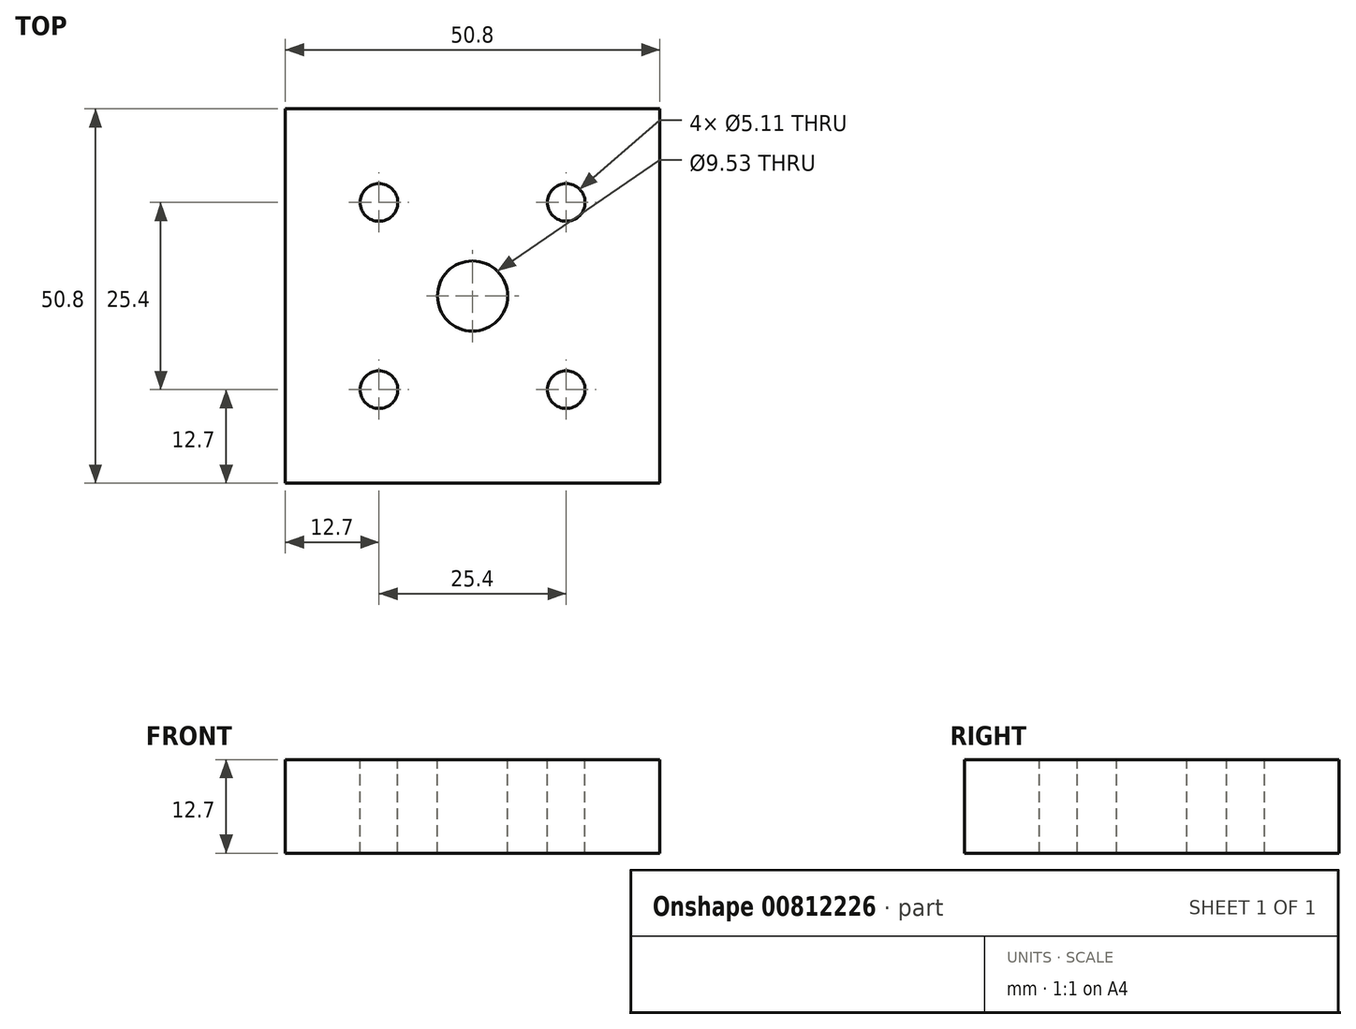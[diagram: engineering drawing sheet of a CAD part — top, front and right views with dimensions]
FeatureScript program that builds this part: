
annotation { "Feature Type Name" : "Feature", "Feature Type Description" : "" }
export const myFeature = defineFeature(function(context is Context, id is Id, definition is map)
    precondition{}
    {
        {
            var Q0;
            Q0=qCreatedBy(makeId("Front.planeOp"),FACE);
            var sketch = newSketch(context, id + "F0", { "sketchPlane" : qUnion([Q0])});
            skLineSegment(sketch, "E0.bottom", {"start": v(-25.4, 0) * mm, "end": v(25.4, 0) * mm});
            skLineSegment(sketch, "E0.top", {"start": v(-25.4, 12.7) * mm, "end": v(25.4, 12.7) * mm});
            skLineSegment(sketch, "E0.left", {"start": v(-25.4, 0) * mm, "end": v(-25.4, 12.7) * mm});
            skLineSegment(sketch, "E0.right", {"start": v(25.4, 0) * mm, "end": v(25.4, 12.7) * mm});
            skPoint(sketch, "E0.middle", {"position": v(0, 6.35) * mm});
            skSolve(sketch);
        }
        {
            var Q0;
            Q0 = qSketchRegion(id + "F0", true);
            extrude(context, id + "F1", {"entities" : qUnion([Q0]), "depth" : 50.8 * mm, "offsetDistance" : 25.4 * mm});
        }
        {
            var Q0;
            Q0=makeQuery(id+"F1.opExtrude","SWEPT_FACE",FACE,{"disambiguationData":[OSD([sQuery(id+"F0.wireOp",EDGE,"E0.top")])]});
            var sketch = newSketch(context, id + "F2", { "sketchPlane" : qUnion([Q0])});
            skLineSegment(sketch, "E1.bottom", {"start": v(-12.7, -12.7) * mm, "end": v(12.7, -12.7) * mm, "construction": true});
            skLineSegment(sketch, "E1.top", {"start": v(-12.7, -38.1) * mm, "end": v(12.7, -38.1) * mm, "construction": true});
            skLineSegment(sketch, "E1.left", {"start": v(-12.7, -12.7) * mm, "end": v(-12.7, -38.1) * mm, "construction": true});
            skLineSegment(sketch, "E1.right", {"start": v(12.7, -12.7) * mm, "end": v(12.7, -38.1) * mm, "construction": true});
            skPoint(sketch, "E1.middle", {"position": v(0, -25.4) * mm});
            skPoint(sketch, "E1.middle.positionSnap0", {"position": v(-25.4, -25.4) * mm});
            skPoint(sketch, "E1.centerSnap0", {"position": v(-25.4, -25.4) * mm});
            skCircle(sketch, "E2", {"center": v(-12.7, -12.7) * mm, "radius": 2.55 * mm});
            skCircle(sketch, "E3", {"center": v(-12.7, -38.1) * mm, "radius": 2.55 * mm});
            skCircle(sketch, "E4", {"center": v(12.7, -38.1) * mm, "radius": 2.55 * mm});
            skCircle(sketch, "E5", {"center": v(12.7, -12.7) * mm, "radius": 2.55 * mm});
            skCircle(sketch, "E6", {"center": v(0, -25.4) * mm, "radius": 4.76 * mm});
            skSolve(sketch);
        }
        {
            var Q0;
            Q0 = qSketchRegion(id + "F2", true);
            extrude(context, id + "F3", {"entities" : qUnion([Q0]), "operationType" : NewBodyOperationType.REMOVE, "endBound" : BoundingType.THROUGH_ALL, "oppositeDirection" : true, "depth" : 25.4 * mm, "offsetDistance" : 25.4 * mm});
        }
        {
            var Q0;
            Q0=makeQuery(id+"F1.opExtrude","SWEPT_FACE",FACE,{"disambiguationData":[OSD([sQuery(id+"F0.wireOp",EDGE,"E0.top")])]});
            var sketch = newSketch(context, id + "F4", { "sketchPlane" : qUnion([Q0])});
            skLineSegment(sketch, "E7.bottom", {"start": v(-25.4, 0) * mm, "end": v(25.4, 0) * mm});
            skLineSegment(sketch, "E7.top", {"start": v(-25.4, -50.8) * mm, "end": v(25.4, -50.8) * mm});
            skLineSegment(sketch, "E7.left", {"start": v(-25.4, 0) * mm, "end": v(-25.4, -50.8) * mm});
            skLineSegment(sketch, "E7.right", {"start": v(25.4, 0) * mm, "end": v(25.4, -50.8) * mm});
            skPoint(sketch, "E7.middle", {"position": v(0, -25.4) * mm});
            skCircle(sketch, "E8", {"center": v(0, -25.4) * mm, "radius": 9.53 * mm});
            skCircle(sketch, "E9", {"center": v(12.7, -12.7) * mm, "radius": 4.76 * mm});
            skCircle(sketch, "E10", {"center": v(-12.7, -12.7) * mm, "radius": 4.76 * mm});
            skCircle(sketch, "E11", {"center": v(12.7, -38.1) * mm, "radius": 4.76 * mm});
            skCircle(sketch, "E12", {"center": v(-12.7, -38.1) * mm, "radius": 4.76 * mm});
            skSolve(sketch);
        }
        {
            var Q0;
            Q0 = qSketchRegion(id + "F4", true);
            extrude(context, id + "F5", {"entities" : qUnion([Q0]), "depth" : 12.7 * mm, "offsetDistance" : 25.4 * mm});
        }
        {
            var Q0;
            Q0=makeQuery(id+"F5.opExtrude","CAP_FACE",FACE,{"disambiguationData":[OSD([sQuery(id+"F4.wireOp",EDGE,"E7.bottom"),sQuery(id+"F4.wireOp",EDGE,"E7.top"),sQuery(id+"F4.wireOp",EDGE,"E7.left"),sQuery(id+"F4.wireOp",EDGE,"E7.right"),sQuery(id+"F4.wireOp",EDGE,"E8"),sQuery(id+"F4.wireOp",EDGE,"E9"),sQuery(id+"F4.wireOp",EDGE,"E10"),sQuery(id+"F4.wireOp",EDGE,"E11"),sQuery(id+"F4.wireOp",EDGE,"E12")])],"isStart":false});
            var sketch = newSketch(context, id + "F6", { "sketchPlane" : qUnion([Q0])});
            skLineSegment(sketch, "E13.bottom", {"start": v(-25.4, 0) * mm, "end": v(25.4, 0) * mm});
            skLineSegment(sketch, "E13.top", {"start": v(-25.4, -50.8) * mm, "end": v(25.4, -50.8) * mm});
            skLineSegment(sketch, "E13.left", {"start": v(-25.4, 0) * mm, "end": v(-25.4, -50.8) * mm});
            skLineSegment(sketch, "E13.right", {"start": v(25.4, 0) * mm, "end": v(25.4, -50.8) * mm});
            skPoint(sketch, "E13.middle", {"position": v(0, -25.4) * mm});
            skCircle(sketch, "E14", {"center": v(0, -25.4) * mm, "radius": 3.18 * mm});
            skCircle(sketch, "E15", {"center": v(-12.7, -12.7) * mm, "radius": 4.76 * mm});
            skCircle(sketch, "E16", {"center": v(-12.7, -38.1) * mm, "radius": 4.76 * mm});
            skCircle(sketch, "E17", {"center": v(12.7, -38.1) * mm, "radius": 4.76 * mm});
            skCircle(sketch, "E18", {"center": v(12.7, -12.7) * mm, "radius": 4.76 * mm});
            skSolve(sketch);
        }
        {
            var Q0;
            Q0 = qSketchRegion(id + "F6", true);
            extrude(context, id + "F7", {"entities" : qUnion([Q0]), "operationType" : NewBodyOperationType.ADD, "depth" : 6.35 * mm, "offsetDistance" : 25.4 * mm});
        }
        {
            var Q0;
            Q0=makeQuery(id+"F7.opExtrude","CAP_FACE",FACE,{"disambiguationData":[OSD([sQuery(id+"F6.wireOp",EDGE,"E13.bottom"),sQuery(id+"F6.wireOp",EDGE,"E13.top"),sQuery(id+"F6.wireOp",EDGE,"E13.left"),sQuery(id+"F6.wireOp",EDGE,"E13.right"),sQuery(id+"F6.wireOp",EDGE,"E14"),sQuery(id+"F6.wireOp",EDGE,"E15"),sQuery(id+"F6.wireOp",EDGE,"E16"),sQuery(id+"F6.wireOp",EDGE,"E17"),sQuery(id+"F6.wireOp",EDGE,"E18")])],"isStart":false});
            var sketch = newSketch(context, id + "F8", { "sketchPlane" : qUnion([Q0])});
            skCircle(sketch, "E19", {"center": v(0, -25.4) * mm, "radius": 2.86 * mm});
            skSolve(sketch);
        }
        {
            var Q0;
            Q0 = qSketchRegion(id + "F8", true);
            extrude(context, id + "F9", {"entities" : qUnion([Q0]), "oppositeDirection" : true, "depth" : 38.1 * mm, "offsetDistance" : 25.4 * mm, "hasSecondDirection" : true, "secondDirectionOppositeDirection" : false, "secondDirectionDepth" : 15.88 * mm});
        }
        {
            var Q0;
            Q0=makeQuery(id+"F9.opExtrude","CAP_FACE",FACE,{"disambiguationData":[OSD([sQuery(id+"F8.wireOp",EDGE,"E19")])],"isStart":true});
            var sketch = newSketch(context, id + "F10", { "sketchPlane" : qUnion([Q0])});
            skCircle(sketch, "E20", {"center": v(0, -25.4) * mm, "radius": 19.05 * mm});
            skSolve(sketch);
        }
        {
            var Q0;
            Q0 = qSketchRegion(id + "F10", true);
            extrude(context, id + "F11", {"entities" : qUnion([Q0]), "operationType" : NewBodyOperationType.ADD, "depth" : 9.52 * mm, "offsetDistance" : 25.4 * mm});
        }
        {
            var Q0;
            Q0=makeQuery(id+"F1.opExtrude","SWEPT_FACE",FACE,{"disambiguationData":[OSD([sQuery(id+"F0.wireOp",EDGE,"E0.top")])]});
            var sketch = newSketch(context, id + "F12", { "sketchPlane" : qUnion([Q0])});
            skCircle(sketch, "E21.cCircle", {"center": v(0, -25.4) * mm, "radius": 4.76 * mm, "construction": true});
            skLineSegment(sketch, "E21.0", {"start": v(4.76, -22.65) * mm, "end": v(4.76, -28.15) * mm});
            skLineSegment(sketch, "E21.1", {"start": v(4.76, -28.15) * mm, "end": v(0, -30.9) * mm});
            skLineSegment(sketch, "E21.2", {"start": v(0, -30.9) * mm, "end": v(-4.76, -28.15) * mm});
            skLineSegment(sketch, "E21.3", {"start": v(-4.76, -28.15) * mm, "end": v(-4.76, -22.65) * mm});
            skLineSegment(sketch, "E21.4", {"start": v(-4.76, -22.65) * mm, "end": v(0, -19.9) * mm});
            skLineSegment(sketch, "E21.5", {"start": v(0, -19.9) * mm, "end": v(4.76, -22.65) * mm});
            skPoint(sketch, "E21.0.midPoint", {"position": v(4.76, -25.4) * mm});
            skCircle(sketch, "E22", {"center": v(0, -25.4) * mm, "radius": 2.86 * mm});
            skSolve(sketch);
        }
        {
            var Q0;
            Q0 = qSketchRegion(id + "F12", true);
            extrude(context, id + "F13", {"entities" : qUnion([Q0]), "depth" : 1.59 * mm, "offsetDistance" : 25.4 * mm});
        }
        {
            var Q0;
            Q0=makeQuery(id+"F13.opExtrude","SWEPT_BODY",BODY,{"disambiguationData":[OSD([sQuery(id+"F12.wireOp",EDGE,"E21.0"),sQuery(id+"F12.wireOp",EDGE,"E21.1"),sQuery(id+"F12.wireOp",EDGE,"E21.2"),sQuery(id+"F12.wireOp",EDGE,"E21.3"),sQuery(id+"F12.wireOp",EDGE,"E21.4"),sQuery(id+"F12.wireOp",EDGE,"E21.5"),sQuery(id+"F12.wireOp",EDGE,"E22")])]});
            deleteBodies(context, id + "F14", {"entities" : qUnion([Q0])});
        }
        {
            var Q0;
            Q0=makeQuery(id+"F9.opExtrude","SWEPT_BODY",BODY,{"disambiguationData":[OSD([sQuery(id+"F8.wireOp",EDGE,"E19")])]});
            deleteBodies(context, id + "F15", {"entities" : qUnion([Q0])});
        }
        {
            var Q0;
            Q0=makeQuery(id+"F5.opExtrude","SWEPT_BODY",BODY,{"disambiguationData":[OSD([sQuery(id+"F4.wireOp",EDGE,"E7.bottom"),sQuery(id+"F4.wireOp",EDGE,"E7.top"),sQuery(id+"F4.wireOp",EDGE,"E7.left"),sQuery(id+"F4.wireOp",EDGE,"E7.right"),sQuery(id+"F4.wireOp",EDGE,"E8"),sQuery(id+"F4.wireOp",EDGE,"E9"),sQuery(id+"F4.wireOp",EDGE,"E10"),sQuery(id+"F4.wireOp",EDGE,"E11"),sQuery(id+"F4.wireOp",EDGE,"E12")])]});
            deleteBodies(context, id + "F16", {"entities" : qUnion([Q0])});
        }
    });
